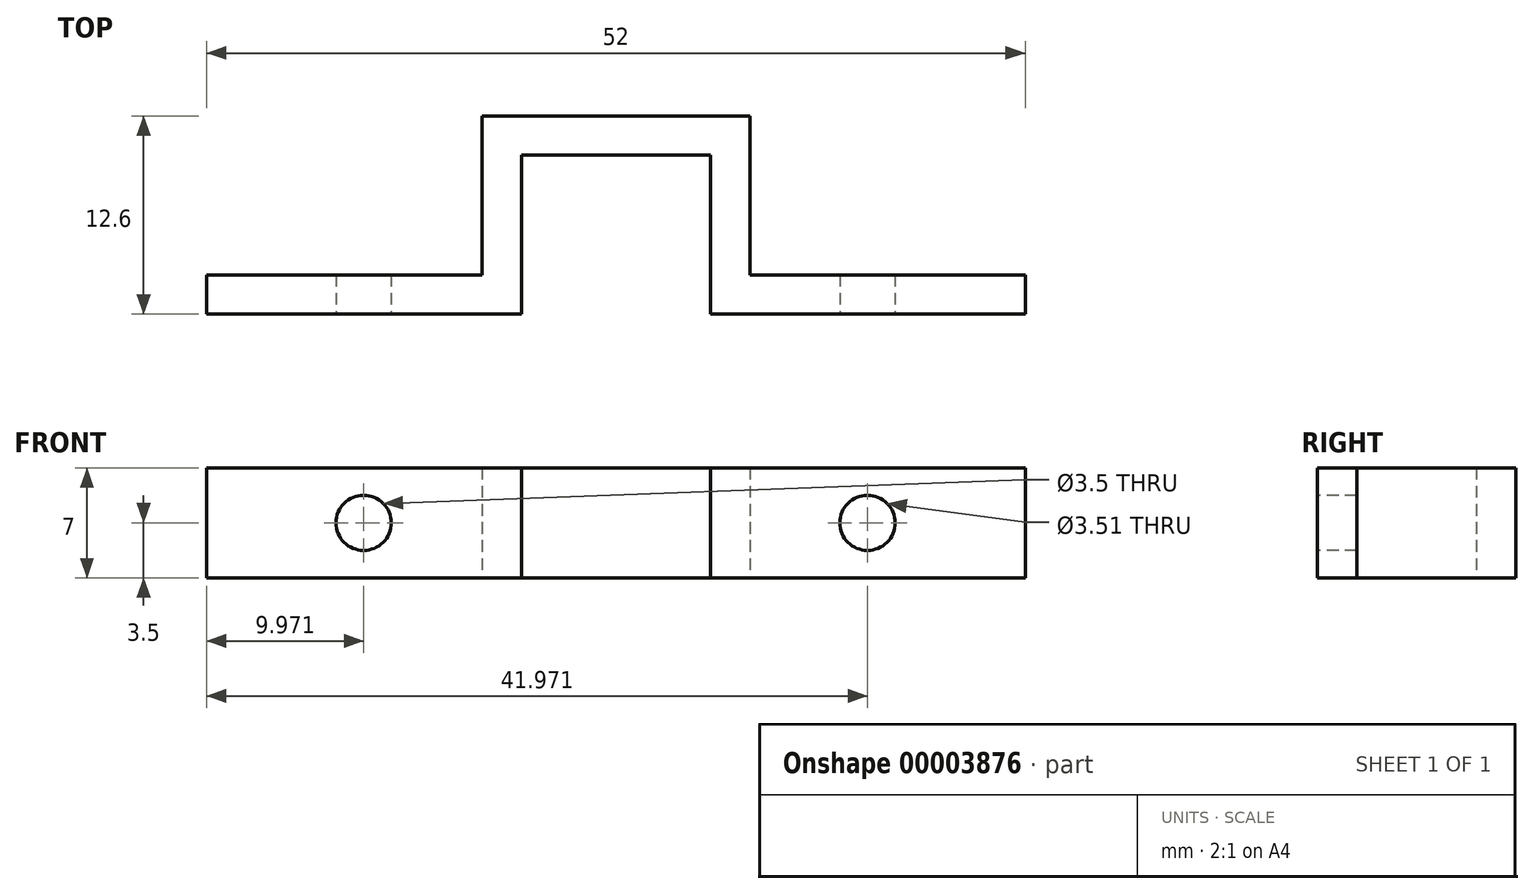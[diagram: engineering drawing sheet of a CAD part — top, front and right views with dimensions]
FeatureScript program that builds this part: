
annotation { "Feature Type Name" : "Feature", "Feature Type Description" : "" }
export const myFeature = defineFeature(function(context is Context, id is Id, definition is map)
    precondition{}
    {
        {
            var Q0;
            Q0=qCreatedBy(makeId("Top.planeOp"),FACE);
            var sketch = newSketch(context, id + "F0", { "sketchPlane" : qUnion([Q0])});
            skLineSegment(sketch, "E0", {"start": v(-20.82, 0) * mm, "end": v(-10.82, 0) * mm});
            skPoint(sketch, "E1", {"position": v(1.18, 0) * mm});
            skPoint(sketch, "E2", {"position": v(-10.82, 0) * mm});
            skPoint(sketch, "E3", {"position": v(-20.82, 0) * mm});
            skPoint(sketch, "E4", {"position": v(11.18, 0) * mm});
            skLineSegment(sketch, "E5", {"start": v(1.18, 0) * mm, "end": v(1.18, 10.1) * mm});
            skLineSegment(sketch, "E6", {"start": v(1.18, 10.1) * mm, "end": v(-10.82, 10.1) * mm});
            skLineSegment(sketch, "E7", {"start": v(-10.82, 10.1) * mm, "end": v(-10.82, 0) * mm});
            skPoint(sketch, "E8", {"position": v(-30.82, 0) * mm});
            skLineSegment(sketch, "E9", {"start": v(-20.82, 0) * mm, "end": v(-30.82, 0) * mm});
            skLineSegment(sketch, "E10", {"start": v(-13.32, 0) * mm, "end": v(-13.32, 12.6) * mm});
            skLineSegment(sketch, "E11", {"start": v(-13.32, 12.6) * mm, "end": v(3.68, 12.6) * mm});
            skLineSegment(sketch, "E12", {"start": v(3.68, 12.6) * mm, "end": v(3.68, 0) * mm});
            skLineSegment(sketch, "E13.trimOffspring", {"start": v(1.18, 0) * mm, "end": v(21.18, 0) * mm});
            skLineSegment(sketch, "E14", {"start": v(-30.82, 0) * mm, "end": v(-30.82, 2.5) * mm});
            skLineSegment(sketch, "E15", {"start": v(-30.82, 2.5) * mm, "end": v(-10.82, 2.5) * mm});
            skLineSegment(sketch, "E16.trimOffspring", {"start": v(1.18, 2.5) * mm, "end": v(21.18, 2.5) * mm});
            skLineSegment(sketch, "E17", {"start": v(11.18, 0) * mm, "end": v(11.18, 2.5) * mm, "construction": true});
            skLineSegment(sketch, "E18", {"start": v(-20.82, 0) * mm, "end": v(-20.82, 2.5) * mm, "construction": true});
            skPoint(sketch, "E19", {"position": v(21.18, 0) * mm});
            skLineSegment(sketch, "E20", {"start": v(21.18, 0) * mm, "end": v(21.18, 2.5) * mm});
            skPoint(sketch, "E21.end.orphan", {"position": v(30.23, 0) * mm});
            skPoint(sketch, "E21.start.orphan", {"position": v(30.23, 2.5) * mm});
            skSolve(sketch);
        }
        {
            var Q0;
            {var subQ4=sQuery(id+"F0.wireOp",EDGE,"E0");var subQ7=sQuery(id+"F0.wireOp",EDGE,"E9");var subQ8=sQuery(id+"F0.wireOp",EDGE,"E20");var subQ9=sQuery(id+"F0.wireOp",EDGE,"E13.trimOffspring");var subQ15=sQuery(id+"F0.wireOp",EDGE,"E7");var subQ18=makeQuery(id+"F0.imprint","INTERSECT",VERTEX,{"derivedFrom":[subQ4,subQ15]});var subQ19=sQuery(id+"F0.wireOp",EDGE,"E5");var subQ22=makeQuery(id+"F0.imprint","INTERSECT",VERTEX,{"derivedFrom":[subQ19,subQ9]});var subQ24=sQuery(id+"F0.wireOp",EDGE,"E6");Q0=qUnion([makeQuery(id+"F0.imprint","IMPRINT",FACE,{"disambiguationData":[TD([[makeQuery(id+"F0.imprint","IMPRINT",EDGE,{"derivedFrom":subQ7}),-1.0]])]}),makeQuery(id+"F0.imprint","IMPRINT",FACE,{"disambiguationData":[TD([[makeQuery(id+"F0.imprint","IMPRINT",EDGE,{"derivedFrom":subQ8}),1.0]])]}),makeQuery(id+"F0.imprint","IMPRINT",FACE,{"disambiguationData":[TD([[makeQuery(id+"F0.imprint","IMPRINT",EDGE,{"disambiguationData":[TD([[subQ18,1.0]])],"derivedFrom":subQ4}),1.0]])]}),makeQuery(id+"F0.imprint","IMPRINT",FACE,{"disambiguationData":[TD([[makeQuery(id+"F0.imprint","IMPRINT",EDGE,{"disambiguationData":[TD([[subQ22,-1.0]])],"derivedFrom":subQ19}),-1.0]])]}),makeQuery(id+"F0.imprint","IMPRINT",FACE,{"disambiguationData":[TD([[makeQuery(id+"F0.imprint","IMPRINT",EDGE,{"derivedFrom":subQ24}),-1.0]])]})]);}
            extrude(context, id + "F1", {"entities" : qUnion([Q0]), "depth" : 7 * mm});
        }
        {
            var Q0;
            Q0=qCreatedBy(makeId("Front.planeOp"),FACE);
            var sketch = newSketch(context, id + "F2", { "sketchPlane" : qUnion([Q0])});
            skPoint(sketch, "E22", {"position": v(11.15, 0) * mm});
            skPoint(sketch, "E23", {"position": v(-20.85, 0) * mm});
            skPoint(sketch, "E24", {"position": v(11.15, 3.5) * mm});
            skCircle(sketch, "E25", {"center": v(11.15, 3.5) * mm, "radius": 1.75 * mm});
            skPoint(sketch, "E26", {"position": v(-20.85, 3.5) * mm});
            skCircle(sketch, "E27", {"center": v(-20.85, 3.5) * mm, "radius": 1.75 * mm});
            skSolve(sketch);
        }
        {
            var Q0;
            {Q0=qUnion([makeQuery(id+"F2.imprint","IMPRINT",FACE,{"disambiguationData":[TD([[makeQuery(id+"F2.imprint","IMPRINT",EDGE,{"derivedFrom":sQuery(id+"F2.wireOp",EDGE,"E25")}),1.0]])]}),makeQuery(id+"F2.imprint","IMPRINT",FACE,{"disambiguationData":[TD([[makeQuery(id+"F2.imprint","IMPRINT",EDGE,{"derivedFrom":sQuery(id+"F2.wireOp",EDGE,"E27")}),1.0]])]})]);}
            extrude(context, id + "F3", {"entities" : qUnion([Q0]), "operationType" : NewBodyOperationType.REMOVE, "oppositeDirection" : true, "depth" : 7 * mm});
        }
    });
